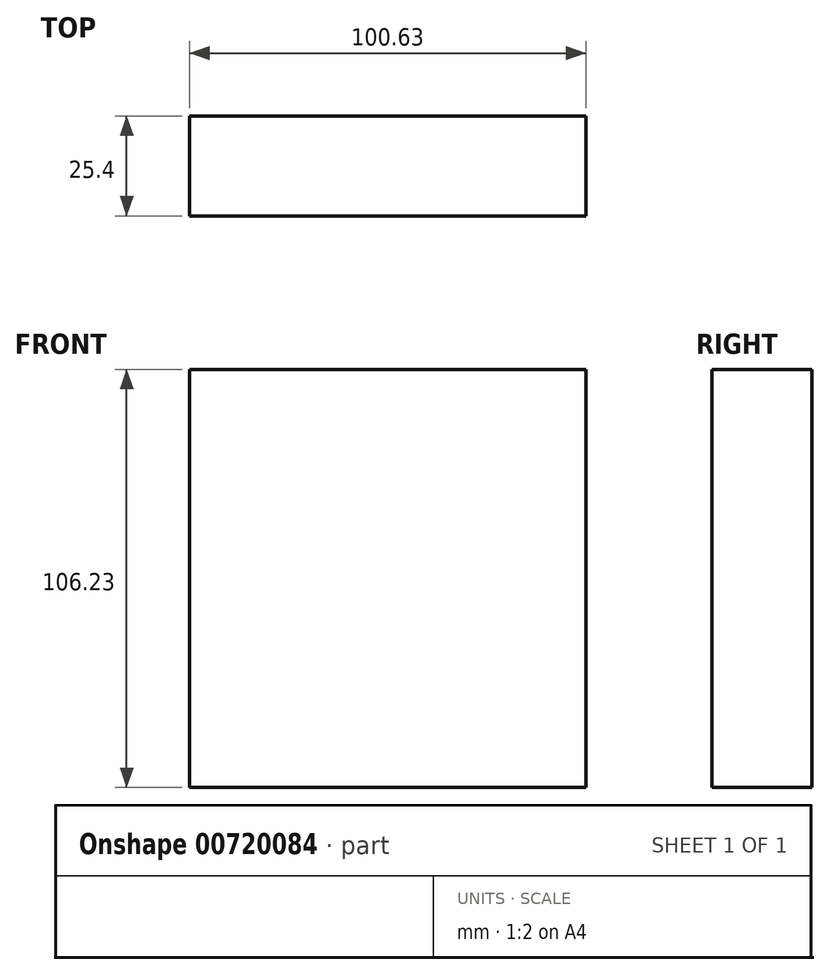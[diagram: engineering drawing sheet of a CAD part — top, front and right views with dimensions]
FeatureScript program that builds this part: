
annotation { "Feature Type Name" : "Feature", "Feature Type Description" : "" }
export const myFeature = defineFeature(function(context is Context, id is Id, definition is map)
    precondition{}
    {
        {
            var Q0;
            Q0=qCreatedBy(makeId("Front.planeOp"),FACE);
            var sketch = newSketch(context, id + "F0", { "sketchPlane" : qUnion([Q0])});
            skLineSegment(sketch, "E0.bottom", {"start": v(-63.14, 87.73) * mm, "end": v(37.49, 87.73) * mm});
            skLineSegment(sketch, "E0.top", {"start": v(-63.14, -18.5) * mm, "end": v(37.49, -18.5) * mm});
            skLineSegment(sketch, "E0.left", {"start": v(-63.14, 87.73) * mm, "end": v(-63.14, -18.5) * mm});
            skLineSegment(sketch, "E0.right", {"start": v(37.49, 87.73) * mm, "end": v(37.49, -18.5) * mm});
            skSolve(sketch);
        }
        {
            var Q0;
            Q0=makeQuery(id+"F0.imprint","IMPRINT",FACE,{"disambiguationData":[TD([[makeQuery(id+"F0.imprint","IMPRINT",EDGE,{"derivedFrom":sQuery(id+"F0.wireOp",EDGE,"E0.bottom")}),-1.0]])]});
            extrude(context, id + "F1", {"entities" : qUnion([Q0]), "depth" : 25.4 * mm, "offsetDistance" : 25.4 * mm});
        }
    });
